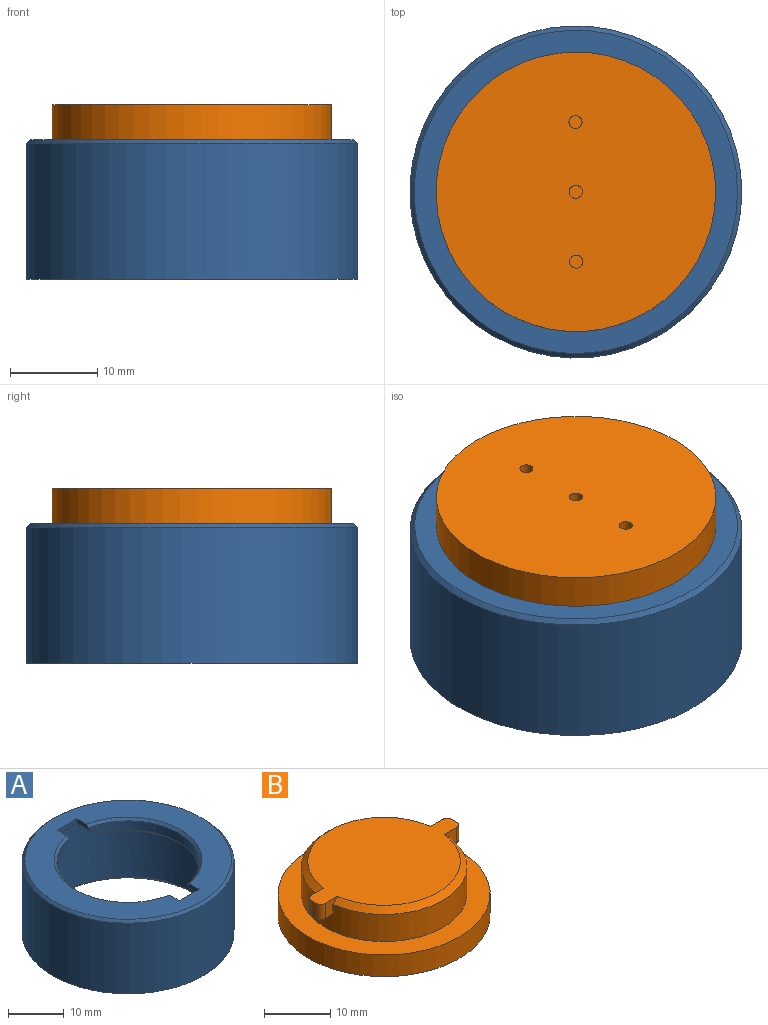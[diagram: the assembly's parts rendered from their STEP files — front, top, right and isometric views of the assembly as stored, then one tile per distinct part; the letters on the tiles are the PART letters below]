
ASSEMBLY  parts=2 mates=1
PART A: 30 faces, bbox 38x38x16 mm
  f0: plane 5x1mm, normal (0,1,0), area 5mm2, adj f4,f16,f17,f29
  f1: plane 5x1mm, normal (0,-1,0), area 5mm2, adj f4,f18,f19,f26
  f2: plane 29.24x9.5mm, normal (0,0,-1), area 89.3mm2, adj f10,f13,f20,f22
  f3: plane 29.24x9.5mm, normal (0,0,-1), area 89.3mm2, adj f6,f10,f21,f23
  f4: plane 37x37mm, normal (0,0,1), area 500.4mm2, adj f0,f1,f7,f14,f15,f16,f17,f18
  f5: cylinder r=12.75mm len=25.01mm, axis (0,0,1), area 65.3mm2, adj f6,f7,f17,f18,f21,f23
  f6: cone r=13.25mm half-angle=45deg, axis (0,0,-1), area 20.1mm2, adj f3,f5,f21,f23
  f7: cone r=12.75mm half-angle=45deg, axis (0,0,1), area 25.3mm2, adj f4,f5,f17,f18
  f8: cylinder r=19mm len=38mm, axis (0,0,-1), area 1850.4mm2, adj f9,f15
  f9: plane 38x38mm, normal (0,0,-1), area 226.2mm2, adj f8,f11
  f10: cylinder r=16mm len=32mm, axis (0,0,-1), area 1245.2mm2, adj f2,f3,f11,f20,f21,f22,f23,f24
  f11: cone r=17mm half-angle=45deg, axis (0,0,-1), area 146.6mm2, adj f9,f10
  f12: cylinder r=12.75mm len=25.01mm, axis (0,0,1), area 65.3mm2, adj f13,f14,f16,f19,f20,f22
  f13: cone r=13.25mm half-angle=45deg, axis (0,0,-1), area 20.1mm2, adj f2,f12,f20,f22
  f14: cone r=12.75mm half-angle=45deg, axis (0,0,1), area 25.3mm2, adj f4,f12,f16,f19
  f15: cone r=18.5mm half-angle=45deg, axis (0,0,-1), area 83.3mm2, adj f4,f8
  f16: plane 3x1mm, normal (1,0,0), area 2.9mm2, adj f0,f4,f12,f14,f20
  f17: plane 3x1mm, normal (-1,0,0), area 2.9mm2, adj f0,f4,f5,f7,f21
  f18: plane 3x1mm, normal (-1,0,0), area 2.9mm2, adj f1,f4,f5,f7,f23
  f19: plane 3x1mm, normal (1,0,0), area 2.9mm2, adj f1,f4,f12,f14,f22
  f20: plane 4.03x4.03mm, normal (0.45,0,-0.89), area 14.8mm2, adj f2,f10,f12,f13,f16,f27
  f21: plane 4.03x4.03mm, normal (-0.45,0,-0.89), area 14.8mm2, adj f3,f5,f6,f10,f17,f28
  f22: plane 4.03x4.03mm, normal (0.45,0,-0.89), area 14.8mm2, adj f2,f10,f12,f13,f19,f25
  f23: plane 4.03x4.03mm, normal (-0.45,0,-0.89), area 14.8mm2, adj f3,f5,f6,f10,f18,f24
  f24: plane 1.47x0.73mm, normal (0,1,0), area 0.5mm2, adj f10,f23,f26
  f25: plane 1.47x0.73mm, normal (0,1,0), area 0.5mm2, adj f10,f22,f26
  f26: plane 7.94x0.5mm, normal (0,0,-1), area 2.7mm2, adj f1,f10,f24,f25
  f27: plane 1.47x0.73mm, normal (0,-1,0), area 0.5mm2, adj f10,f20,f29
  f28: plane 1.47x0.73mm, normal (0,-1,0), area 0.5mm2, adj f10,f21,f29
  f29: plane 7.94x0.5mm, normal (0,0,-1), area 2.7mm2, adj f0,f10,f27,f28
PART B: 25 faces, bbox 32x32x10 mm
  f0: cone r=11.5mm half-angle=45deg, axis (0,0,-1), area 49.1mm2, adj f1,f2,f14,f20
  f1: cylinder r=12.5mm len=25mm, axis (0,0,-1), area 381.9mm2, adj f0,f5,f12,f13,f14,f18,f19,f20
  f2: plane 30x23mm, normal (0,0,1), area 435.8mm2, adj f0,f12,f13,f14,f15,f16,f17,f19
  f3: cylinder r=16mm len=32mm, axis (0,0,1), area 402.1mm2, adj f4,f5
  f4: plane 32x32mm, normal (0,0,-1), area 798.9mm2, adj f3,f6,f8,f10
  f5: plane 32x32mm, normal (0,0,1), area 313.4mm2, adj f1,f3
  f6: cylinder r=0.75mm len=2mm, axis (0,0,-1), area 9.4mm2, adj f4,f7
  f7: plane 1.5x1.5mm, normal (0,0,-1), area 1.8mm2, adj f6
  f8: cylinder r=0.75mm len=2mm, axis (0,0,-1), area 9.4mm2, adj f4,f9
  f9: plane 1.5x1.5mm, normal (0,0,-1), area 1.8mm2, adj f8
  f10: cylinder r=0.75mm len=2mm, axis (0,0,-1), area 9.4mm2, adj f4,f11
  f11: plane 1.5x1.5mm, normal (0,0,-1), area 1.8mm2, adj f10
  f12: cone r=11.5mm half-angle=45deg, axis (0,0,-1), area 49.1mm2, adj f1,f2,f13,f19
  f13: plane 2.81x2.6mm, normal (0,-1,0), area 5mm2, adj f1,f2,f12,f15,f18
  f14: plane 2.81x2.6mm, normal (0,1,0), area 5mm2, adj f0,f1,f2,f16,f18
  f15: cylinder r=1mm len=2.8mm, axis (0,0,1), area 4.4mm2, adj f2,f13,f17,f18
  f16: cylinder r=1mm len=2.8mm, axis (0,0,1), area 4.4mm2, adj f2,f14,f17,f18
  f17: plane 2.8x1mm, normal (-1,0,0), area 2.8mm2, adj f2,f15,f16,f18
  f18: plane 3x2.59mm, normal (0,0,-1), area 7.2mm2, adj f1,f13,f14,f15,f16,f17
  f19: plane 2.81x2.6mm, normal (0,-1,0), area 5mm2, adj f1,f2,f12,f21,f24
  f20: plane 2.81x2.6mm, normal (0,1,0), area 5mm2, adj f0,f1,f2,f23,f24
  f21: cylinder r=1mm len=2.8mm, axis (0,0,1), area 4.4mm2, adj f2,f19,f22,f24
  f22: plane 2.8x1mm, normal (1,0,0), area 2.8mm2, adj f2,f21,f23,f24
  f23: cylinder r=1mm len=2.8mm, axis (0,0,1), area 4.4mm2, adj f2,f20,f22,f24
  f24: plane 3x2.59mm, normal (0,0,-1), area 7.2mm2, adj f1,f19,f20,f21,f22,f23
PLACE A t=(0,0,-16)mm
PLACE B rot(axis=(-0.71,-0.71,0),180deg) t=(0,0,0)mm
MATE revolute A.f5 <-> B.f0  axis (0,0,1) through (0,0,0)mm
